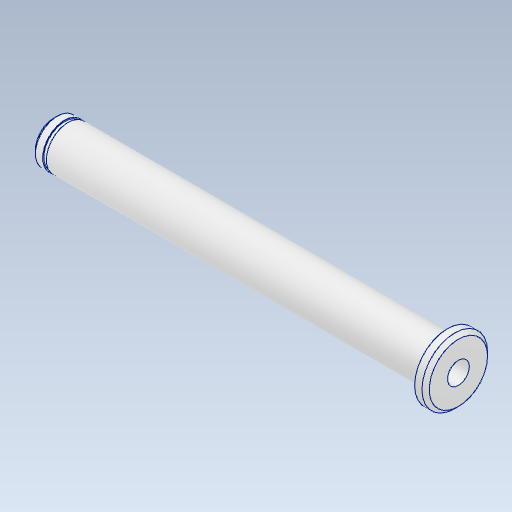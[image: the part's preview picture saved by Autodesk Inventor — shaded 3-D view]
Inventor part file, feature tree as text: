
AUTODESK INVENTOR PART (.ipt)
format: ipt  version: 2024 (Build 280153000, 153)  size: 204,288 bytes
history: native  units: mm
features: other x4, chamfer x1, extrude x1, sketch x1
ambient origin geometry x8: Origin, YZ Plane, XZ Plane, XY Plane, X Axis, Y Axis, Z Axis, Center Point
bodies: Body1 (feature_tree)
feature tree (7):
  other  "_bridseye_sketch.ipt"
  chamfer  "面取り1"  Distance=10.0mm
  extrude  "押し出し2"  Depth=0.5mm TaperAngle=45.0deg
  other  "ソリッド18::_bridseye_sketch.ipt"
  other  "TaggingFeature1"
  other  "top_elbowUnit"
  sketch  "スケッチ3"
